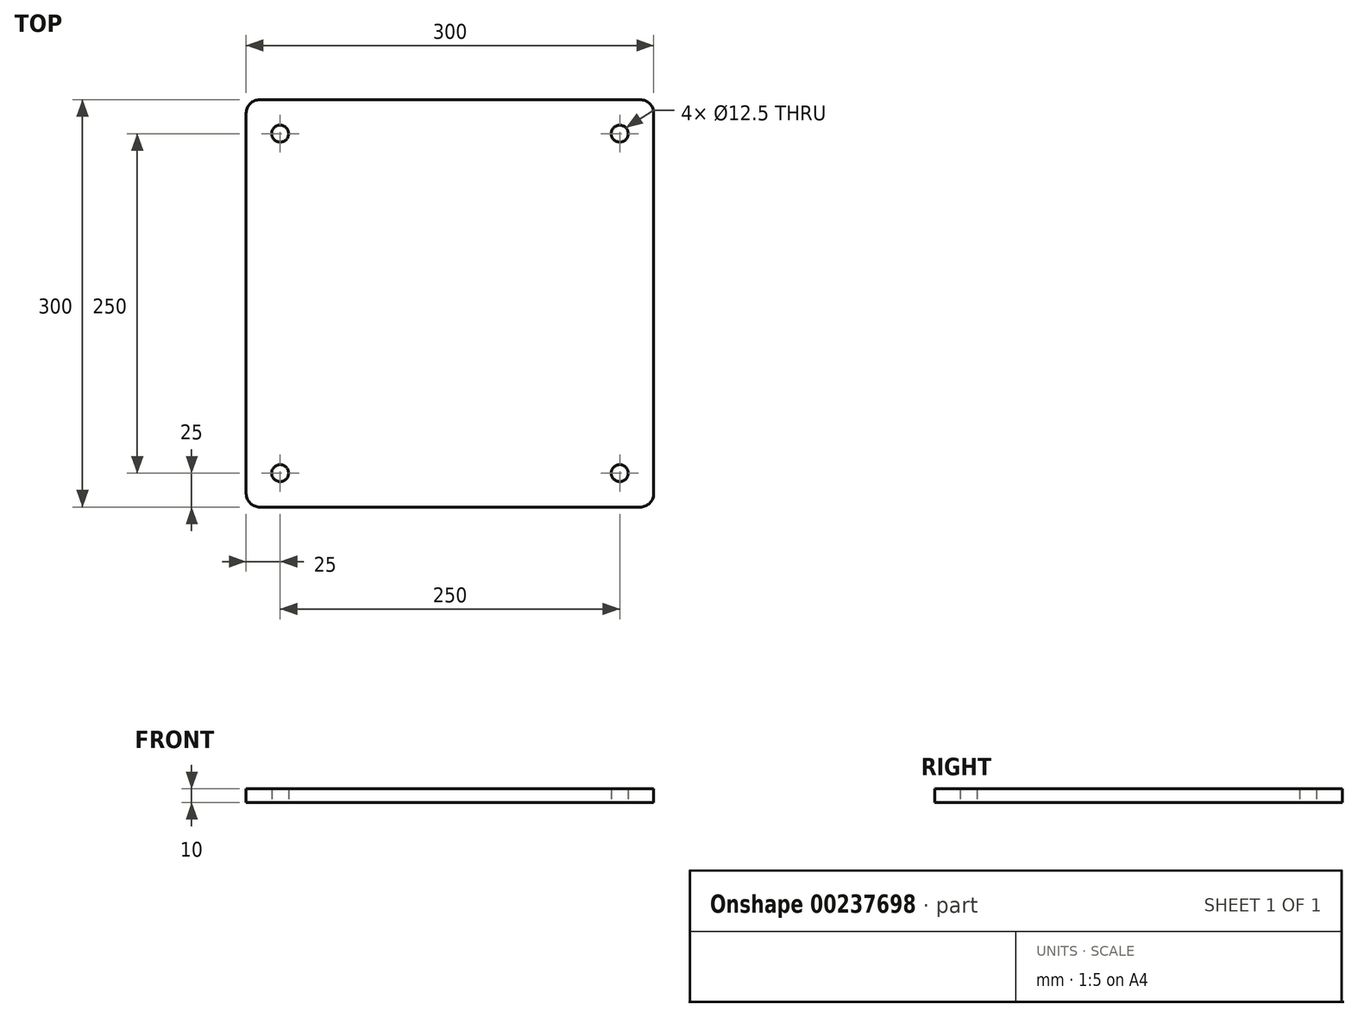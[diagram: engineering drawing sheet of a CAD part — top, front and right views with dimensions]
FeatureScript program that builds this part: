
annotation { "Feature Type Name" : "Feature", "Feature Type Description" : "" }
export const myFeature = defineFeature(function(context is Context, id is Id, definition is map)
    precondition{}
    {
        {
            var Q0;
            Q0=qCreatedBy(makeId("Top.planeOp"),FACE);
            var sketch = newSketch(context, id + "F0", { "sketchPlane" : qUnion([Q0])});
            skLineSegment(sketch, "E0.bottom", {"start": v(140, 150) * mm, "end": v(-140, 150) * mm});
            skLineSegment(sketch, "E0.top", {"start": v(140, -150) * mm, "end": v(-140, -150) * mm});
            skLineSegment(sketch, "E0.left", {"start": v(150, 140) * mm, "end": v(150, -140) * mm});
            skLineSegment(sketch, "E0.right", {"start": v(-150, 140) * mm, "end": v(-150, -140) * mm});
            skPoint(sketch, "E0.middle", {"position": v(0, 0) * mm});
            skPoint(sketch, "E1.visualSharp", {"position": v(-150, 150) * mm});
            skArc(sketch, "E1.filletArc", {"start": v(-140, 150) * mm, "mid": v(-147.07, 147.07) * mm, "end": v(-150, 140) * mm});
            skPoint(sketch, "E2.visualSharp", {"position": v(150, 150) * mm});
            skArc(sketch, "E2.filletArc", {"start": v(150, 140) * mm, "mid": v(147.07, 147.07) * mm, "end": v(140, 150) * mm});
            skPoint(sketch, "E3.visualSharp", {"position": v(150, -150) * mm});
            skArc(sketch, "E3.filletArc", {"start": v(140, -150) * mm, "mid": v(147.07, -147.07) * mm, "end": v(150, -140) * mm});
            skPoint(sketch, "E4.visualSharp", {"position": v(-150, -150) * mm});
            skArc(sketch, "E4.filletArc", {"start": v(-150, -140) * mm, "mid": v(-147.07, -147.07) * mm, "end": v(-140, -150) * mm});
            skCircle(sketch, "E5", {"center": v(-125, 125) * mm, "radius": 6.25 * mm});
            skCircle(sketch, "E6.0.1.0", {"center": v(-125, -125) * mm, "radius": 6.25 * mm});
            skCircle(sketch, "E6.1.0.0", {"center": v(125, 125) * mm, "radius": 6.25 * mm});
            skCircle(sketch, "E6.1.1.0", {"center": v(125, -125) * mm, "radius": 6.25 * mm});
            skLineSegment(sketch, "E6.direction1", {"start": v(-125, 125) * mm, "end": v(125, 125) * mm, "construction": true});
            skLineSegment(sketch, "E6.direction2", {"start": v(-125, 125) * mm, "end": v(-125, -125) * mm, "construction": true});
            skSolve(sketch);
        }
        {
            var Q0;
            Q0=makeQuery(id+"F0.imprint","IMPRINT",FACE,{"disambiguationData":[TD([[makeQuery(id+"F0.imprint","IMPRINT",EDGE,{"derivedFrom":sQuery(id+"F0.wireOp",EDGE,"E0.bottom")}),1.0]])]});
            extrude(context, id + "F1", {"entities" : qUnion([Q0]), "depth" : 10 * mm});
        }
    });
